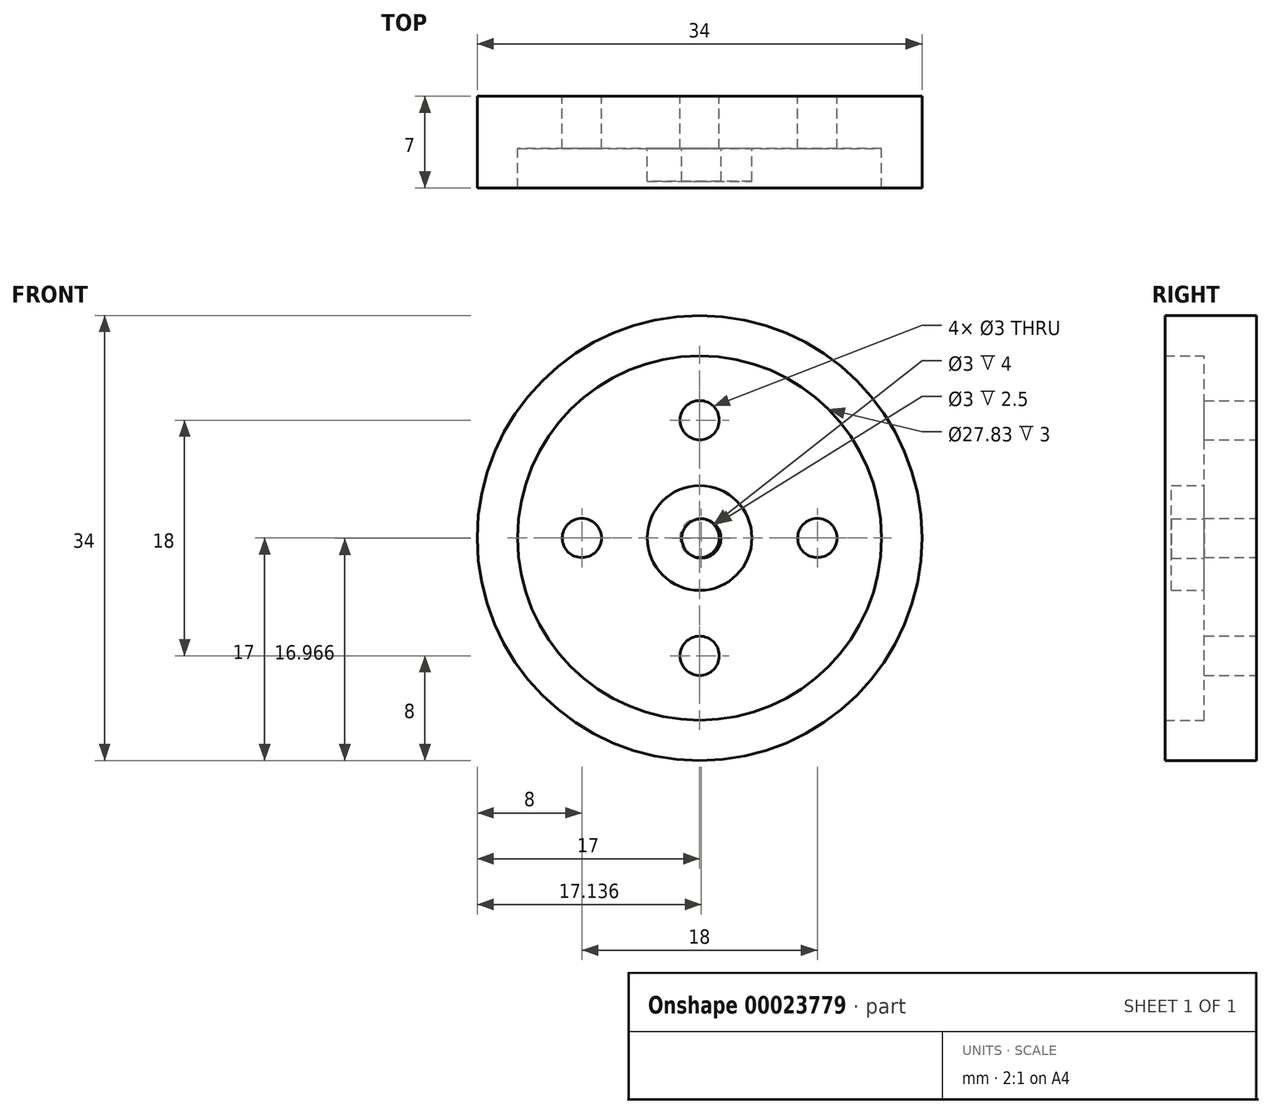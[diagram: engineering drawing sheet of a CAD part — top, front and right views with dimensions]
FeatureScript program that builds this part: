
annotation { "Feature Type Name" : "Feature", "Feature Type Description" : "" }
export const myFeature = defineFeature(function(context is Context, id is Id, definition is map)
    precondition{}
    {
        {
            var Q0;
            Q0=qCreatedBy(makeId("Front.planeOp"),FACE);
            var sketch = newSketch(context, id + "F0", { "sketchPlane" : qUnion([Q0])});
            skCircle(sketch, "E0", {"center": v(0, 0) * mm, "radius": 17 * mm});
            skCircle(sketch, "E1", {"center": v(0, 0) * mm, "radius": 1.5 * mm});
            skCircle(sketch, "E2", {"center": v(0, 0) * mm, "radius": 4 * mm});
            skCircle(sketch, "E3", {"center": v(0, 9) * mm, "radius": 1.5 * mm});
            skCircle(sketch, "E4.1.0", {"center": v(-9, 0) * mm, "radius": 1.5 * mm});
            skCircle(sketch, "E4.2.0", {"center": v(0, -9) * mm, "radius": 1.5 * mm});
            skCircle(sketch, "E4.3.0", {"center": v(9, 0) * mm, "radius": 1.5 * mm});
            skSolve(sketch);
        }
        {
            var Q0;
            Q0=makeQuery(id+"F0.imprint","IMPRINT",FACE,{"disambiguationData":[TD([[makeQuery(id+"F0.imprint","IMPRINT",EDGE,{"derivedFrom":sQuery(id+"F0.wireOp",EDGE,"E0")}),1.0]])]});
            var Q1;
            Q1=makeQuery(id+"F0.imprint","IMPRINT",FACE,{"disambiguationData":[TD([[makeQuery(id+"F0.imprint","IMPRINT",EDGE,{"derivedFrom":sQuery(id+"F0.wireOp",EDGE,"E1")}),-1.0]])]});
            extrude(context, id + "F1", {"entities" : qUnion([Q0, Q1]), "depth" : 4 * mm});
        }
        {
            var Q0;
            Q0=makeQuery(id+"F1.opExtrude","CAP_FACE",FACE,{"disambiguationData":[OSD([sQuery(id+"F0.wireOp",EDGE,"E0"),sQuery(id+"F0.wireOp",EDGE,"E2"),sQuery(id+"F0.wireOp",EDGE,"E3"),sQuery(id+"F0.wireOp",EDGE,"E4.1.0"),sQuery(id+"F0.wireOp",EDGE,"E4.2.0"),sQuery(id+"F0.wireOp",EDGE,"E4.3.0")])],"isStart":false});
            var sketch = newSketch(context, id + "F2", { "sketchPlane" : qUnion([Q0])});
            skLineSegment(sketch, "E5", {"start": v(9.57, 14.05) * mm, "end": v(12.15, 15.57) * mm});
            skLineSegment(sketch, "E6", {"start": v(12.15, 15.57) * mm, "end": v(12.15, 15.57) * mm});
            skLineSegment(sketch, "E7", {"start": v(12.92, 14.93) * mm, "end": v(11.93, 12.1) * mm});
            skLineSegment(sketch, "E8", {"start": v(12.15, 15.57) * mm, "end": v(12.92, 14.93) * mm});
            skCircle(sketch, "E9", {"center": v(0.14, -0.03) * mm, "radius": 1.5 * mm});
            skCircle(sketch, "E10", {"center": v(0, 0) * mm, "radius": 4 * mm});
            skSolve(sketch);
        }
        {
            var Q0;
            Q0 = qSketchRegion(id + "F2", true);
            var Q1;
            Q1=makeQuery(id+"F2.imprint","IMPRINT",FACE,{"disambiguationData":[TD([[makeQuery(id+"F2.imprint","IMPRINT",EDGE,{"derivedFrom":sQuery(id+"F2.wireOp",EDGE,"E10")}),1.0]])]});
            extrude(context, id + "F3", {"entities" : qUnion([Q0, Q1]), "operationType" : NewBodyOperationType.ADD, "depth" : 2.5 * mm});
        }
        {
            var Q0;
            {var subQ0=sQuery(id+"F0.wireOp",EDGE,"E0");var subQ1=sQuery(id+"F0.wireOp",EDGE,"E3");var subQ2=sQuery(id+"F0.wireOp",EDGE,"E4.1.0");var subQ3=sQuery(id+"F0.wireOp",EDGE,"E4.2.0");var subQ4=sQuery(id+"F0.wireOp",EDGE,"E4.3.0");Q0=makeQuery(id+"F3.boolean.opBoolean","SPLIT",FACE,{"disambiguationData":[TD([makeQuery(id+"F1.opExtrude","SWEPT_FACE",FACE,{"disambiguationData":[OSD([subQ0])]})])],"derivedFrom":makeQuery(id+"F1.opExtrude","CAP_FACE",FACE,{"disambiguationData":[OSD([subQ0,sQuery(id+"F0.wireOp",EDGE,"E1"),subQ1,subQ2,subQ3,subQ4])],"isStart":false})});}
            var sketch = newSketch(context, id + "F4", { "sketchPlane" : qUnion([Q0])});
            skCircle(sketch, "E11", {"center": v(0, 0) * mm, "radius": 13.92 * mm});
            skSolve(sketch);
        }
        {
            var Q0;
            Q0=makeQuery(id+"F4.imprint","IMPRINT",FACE,{"disambiguationData":[TD([[makeQuery(id+"F4.imprint","IMPRINT",EDGE,{"derivedFrom":sQuery(id+"F4.wireOp",EDGE,"E11")}),-1.0]])]});
            extrude(context, id + "F5", {"entities" : qUnion([Q0]), "operationType" : NewBodyOperationType.ADD, "depth" : 3 * mm});
        }
    });
